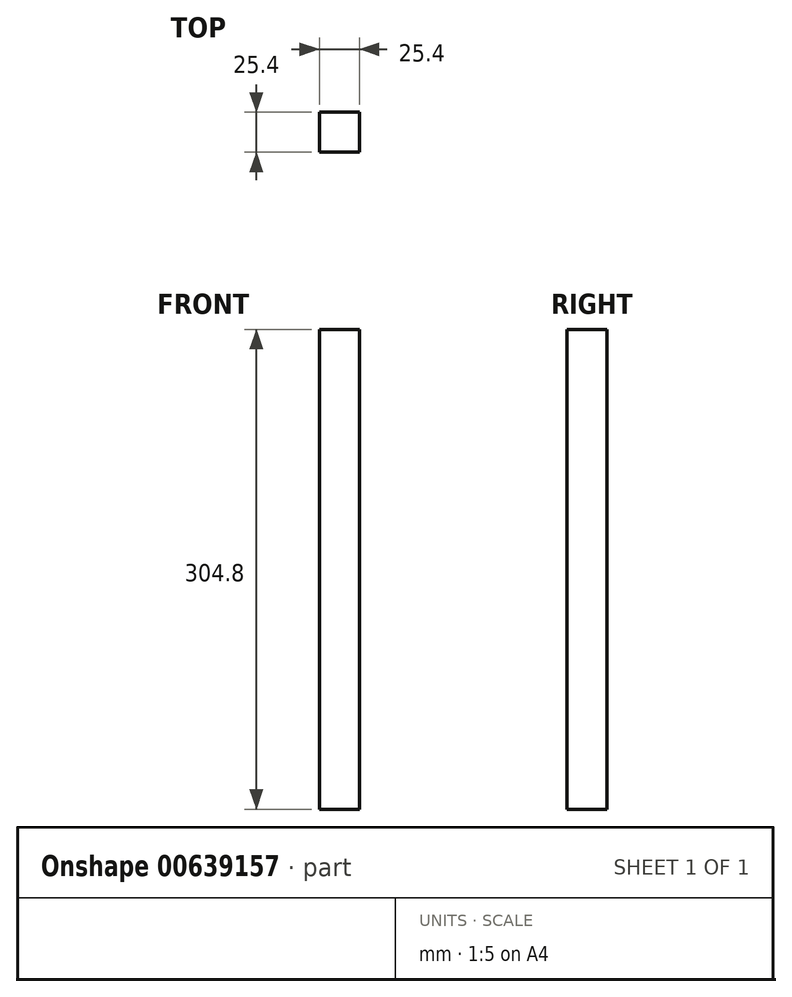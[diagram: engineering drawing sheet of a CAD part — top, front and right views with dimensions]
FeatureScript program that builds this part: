
annotation { "Feature Type Name" : "Feature", "Feature Type Description" : "" }
export const myFeature = defineFeature(function(context is Context, id is Id, definition is map)
    precondition{}
    {
        {
            var Q0;
            Q0=qCreatedBy(makeId("Front.planeOp"),FACE);
            var sketch = newSketch(context, id + "F0", { "sketchPlane" : qUnion([Q0])});
            skLineSegment(sketch, "E0.bottom", {"start": v(0, 147.43) * mm, "end": v(25.4, 147.43) * mm});
            skLineSegment(sketch, "E0.top", {"start": v(0, -157.37) * mm, "end": v(25.4, -157.37) * mm});
            skLineSegment(sketch, "E0.left", {"start": v(0, 147.43) * mm, "end": v(0, -157.37) * mm});
            skLineSegment(sketch, "E0.right", {"start": v(25.4, 147.43) * mm, "end": v(25.4, -157.37) * mm});
            skSolve(sketch);
        }
        {
            var Q0;
            Q0=makeQuery(id+"F0.imprint","IMPRINT",FACE,{"disambiguationData":[TD([[makeQuery(id+"F0.imprint","IMPRINT",EDGE,{"derivedFrom":sQuery(id+"F0.wireOp",EDGE,"E0.bottom")}),-1.0]])]});
            extrude(context, id + "F1", {"entities" : qUnion([Q0]), "depth" : 25.4 * mm, "offsetDistance" : 25.4 * mm});
        }
    });
